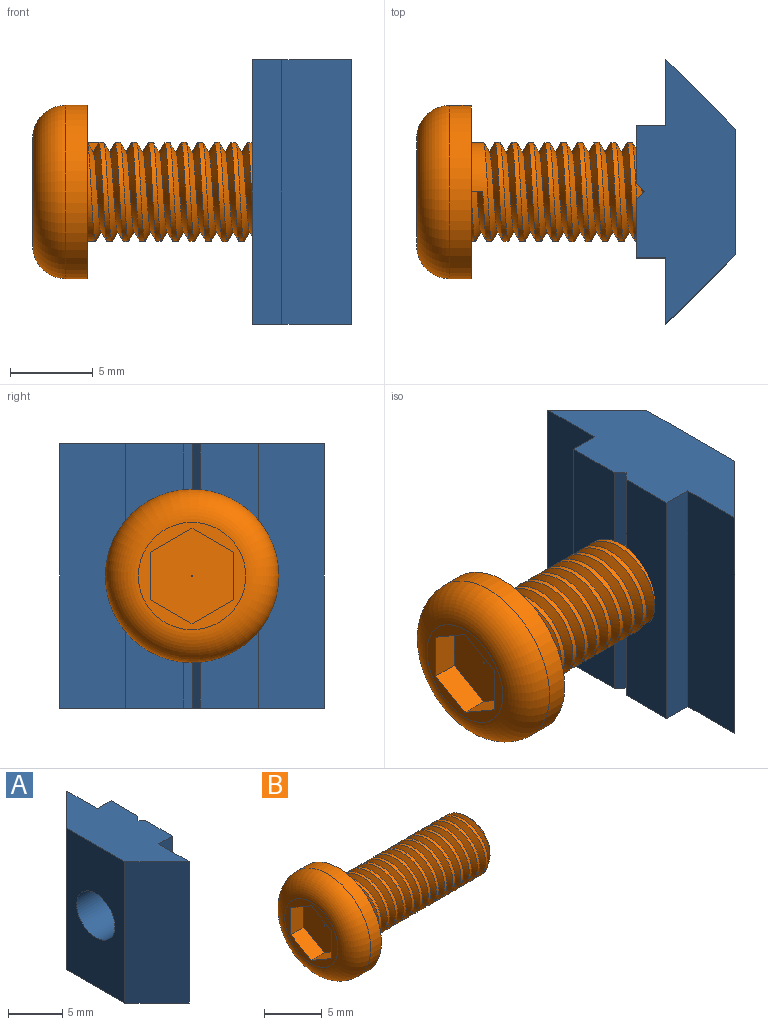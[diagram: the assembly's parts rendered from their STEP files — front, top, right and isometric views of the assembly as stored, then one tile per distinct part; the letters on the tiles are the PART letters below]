
ASSEMBLY  parts=2 mates=1
PART A: 16 faces, bbox 6x16x16 mm
  f0: plane 5.55x0.5mm, normal (0.71,0.71,0), area 3.9mm2, adj f6,f8,f14,f15
  f1: plane 5.55x0.5mm, normal (0.71,-0.71,0), area 3.9mm2, adj f7,f9,f13,f15
  f2: plane 16x7.6mm, normal (-1,0,0), area 102mm2, adj f3,f12,f13,f14,f15
  f3: plane 16x4.2mm, normal (-0.71,-0.71,0), area 95mm2, adj f2,f4,f13,f14
  f4: plane 16x4mm, normal (1,0,0), area 64mm2, adj f3,f5,f13,f14
  f5: plane 16x1.8mm, normal (0,-1,0), area 28.8mm2, adj f4,f6,f13,f14
  f6: plane 16x3.5mm, normal (1,0,0), area 48.7mm2, adj f0,f5,f7,f13,f14,f15
  f7: plane 5.55x0.5mm, normal (0.71,0.71,0), area 3.9mm2, adj f1,f6,f13,f15
  f8: plane 5.55x0.5mm, normal (0.71,-0.71,0), area 3.9mm2, adj f0,f9,f14,f15
  f9: plane 16x3.5mm, normal (1,0,0), area 48.7mm2, adj f1,f8,f10,f13,f14,f15
  f10: plane 16x1.8mm, normal (0,1,0), area 28.8mm2, adj f9,f11,f13,f14
  f11: plane 16x4mm, normal (1,0,0), area 64mm2, adj f10,f12,f13,f14
  f12: plane 16x4.2mm, normal (-0.71,0.71,0), area 95mm2, adj f2,f11,f13,f14
  f13: plane 16x6mm, normal (0,0,1), area 63.7mm2, adj f1,f2,f3,f4,f5,f6,f7,f9
  f14: plane 16x6mm, normal (0,0,-1), area 63.7mm2, adj f0,f2,f3,f4,f5,f6,f8,f9
  f15: cylinder r=2.5mm len=6mm, axis (-1,0,0), area 93.7mm2, adj f0,f1,f2,f6,f7,f8,f9
PART B: 18 faces, bbox 19.7x11.4x11.4 mm
  f0: plane 6.5x6.5mm, normal (-1,0,0), area 11.5mm2, adj f5,f6,f7,f8,f9,f10,f11
  f1: plane 10.5x10.5mm, normal (1,0,0), area 58.3mm2, adj f2,f4
  f2: cylinder r=5.25mm len=10.5mm, axis (-1,0,0), area 42.9mm2, adj f1,f5
  f3: plane 5.02x5.02mm, normal (1,0,0), area 19.5mm2, adj f13,f14,f15,f17
  f4: cylinder r=3mm len=15.5mm, axis (-1,0,0), area 84.8mm2, adj f1,f13,f14,f15,f16
  f5: torus R=3.25mm, axis (-1,0,0), area 89.3mm2, adj f0,f2
  f6: plane 2.5x1.6mm, normal (0,0.5,-0.87), area 4.6mm2, adj f0,f7,f11,f12
  f7: plane 2.5x1.6mm, normal (0,-0.5,-0.87), area 4.6mm2, adj f0,f6,f8,f12
  f8: plane 2.89x1.6mm, normal (0,-1,0), area 4.6mm2, adj f0,f7,f9,f12
  f9: plane 2.5x1.6mm, normal (0,-0.5,0.87), area 4.6mm2, adj f0,f8,f10,f12
  f10: plane 2.5x1.6mm, normal (0,0.5,0.87), area 4.6mm2, adj f0,f9,f11,f12
  f11: plane 2.89x1.6mm, normal (0,1,0), area 4.6mm2, adj f0,f6,f10,f12
  f12: plane 5.77x5mm, normal (-1,0,0), area 21.6mm2, adj f6,f7,f8,f9,f10,f11,f17
  f13: cone r=3mm half-angle=45deg, axis (-1,0,0), area 7mm2, adj f3,f4,f14,f15
  f14: bspline ~16.02x6.93mm, area 181.5mm2, adj f3,f4,f13,f15,f16
  f15: bspline ~16.19x6.93mm, area 186.1mm2, adj f3,f4,f13,f14,f16
  f16: plane 0.7x0.61mm, normal (0,-1,0), area 0.2mm2, adj f4,f14,f15
  f17: cylinder r=0.05mm len=17.7mm, axis (-1,0,0), area 5.6mm2, adj f3,f12
PLACE A rot(axis=(0,0,-1),180deg) t=(9.92,-3.44,-11)mm
PLACE B t=(-3.38,-3.44,-3)mm
MATE fastened B.f2 <-> A.f15  axis (1,0,0) through (15.92,-3.44,-3)mm
